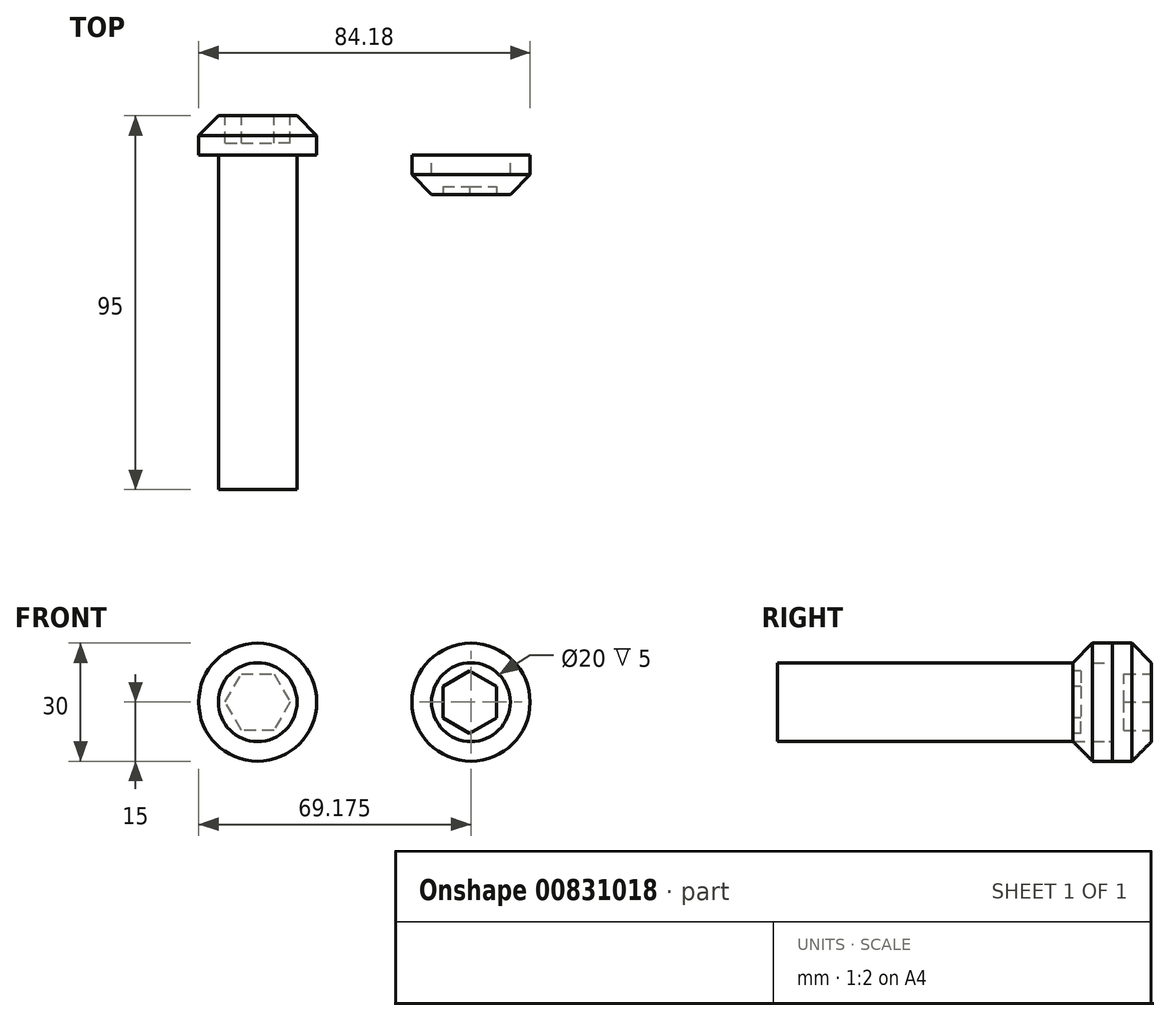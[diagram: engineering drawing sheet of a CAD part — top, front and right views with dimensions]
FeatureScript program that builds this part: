
annotation { "Feature Type Name" : "Feature", "Feature Type Description" : "" }
export const myFeature = defineFeature(function(context is Context, id is Id, definition is map)
    precondition{}
    {
        {
            var Q0;
            Q0=qCreatedBy(makeId("Front.planeOp"),FACE);
            var sketch = newSketch(context, id + "F0", { "sketchPlane" : qUnion([Q0])});
            skCircle(sketch, "E0", {"center": v(0, 0) * mm, "radius": 10 * mm});
            skCircle(sketch, "E1", {"center": v(0, 0) * mm, "radius": 15 * mm});
            skSolve(sketch);
        }
        {
            var Q0;
            Q0=makeQuery(id+"F0.imprint","IMPRINT",FACE,{"disambiguationData":[TD([[makeQuery(id+"F0.imprint","IMPRINT",EDGE,{"derivedFrom":sQuery(id+"F0.wireOp",EDGE,"E0")}),1.0]])]});
            extrude(context, id + "F1", {"entities" : qUnion([Q0]), "depth" : 85 * mm, "offsetDistance" : 25 * mm});
        }
        {
            var Q0;
            Q0 = qSketchRegion(id + "F0", true);
            var Q1;
            Q1=makeQuery(id+"F1.opExtrude","CAP_FACE",FACE,{"disambiguationData":[OSD([sQuery(id+"F0.wireOp",EDGE,"E0")])],"isStart":true});
            extrude(context, id + "F2", {"entities" : qUnion([Q0, Q1]), "operationType" : NewBodyOperationType.ADD, "oppositeDirection" : true, "depth" : 10 * mm, "offsetDistance" : 25 * mm});
        }
        {
            var Q0;
            Q0=qCreatedBy(makeId("Front.planeOp"),FACE);
            var sketch = newSketch(context, id + "F3", { "sketchPlane" : qUnion([Q0])});
            skCircle(sketch, "E2", {"center": v(54.18, 0) * mm, "radius": 10 * mm});
            skCircle(sketch, "E3", {"center": v(54.18, 0) * mm, "radius": 15 * mm});
            skSolve(sketch);
        }
        {
            var Q0;
            Q0=makeQuery(id+"F3.imprint","IMPRINT",FACE,{"disambiguationData":[TD([[makeQuery(id+"F3.imprint","IMPRINT",EDGE,{"derivedFrom":sQuery(id+"F3.wireOp",EDGE,"E2")}),-1.0]])]});
            var Q1;
            Q1=makeQuery(id+"F3.imprint","IMPRINT",FACE,{"disambiguationData":[TD([[makeQuery(id+"F3.imprint","IMPRINT",EDGE,{"derivedFrom":sQuery(id+"F3.wireOp",EDGE,"E2")}),1.0]])]});
            extrude(context, id + "F4", {"entities" : qUnion([Q0, Q1]), "depth" : 10 * mm, "offsetDistance" : 25 * mm});
        }
        {
            var Q0;
            Q0=makeQuery(id+"F3.imprint","IMPRINT",FACE,{"disambiguationData":[TD([[makeQuery(id+"F3.imprint","IMPRINT",EDGE,{"derivedFrom":sQuery(id+"F3.wireOp",EDGE,"E2")}),1.0]])]});
            extrude(context, id + "F5", {"entities" : qUnion([Q0]), "operationType" : NewBodyOperationType.REMOVE, "depth" : 5 * mm, "offsetDistance" : 25 * mm});
        }
        {
            var Q0;
            Q0=makeQuery(id+"F2.opExtrude","CAP_EDGE",EDGE,{"disambiguationData":[OSD([sQuery(id+"F0.wireOp",EDGE,"E1")])],"isStart":false});
            var Q1;
            Q1=makeQuery(id+"F4.opExtrude","CAP_EDGE",EDGE,{"disambiguationData":[OSD([sQuery(id+"F3.wireOp",EDGE,"E3")])],"isStart":false});
            chamfer(context, id + "F6", {"entities" : qUnion([Q0, Q1]), "width" : 5 * mm, "tangentPropagation" : true});
        }
        {
            var Q0;
            Q0=qCreatedBy(makeId("Front.planeOp"),FACE);
            cPlane(context, id + "F7", {"entities" : qUnion([Q0]), "cplaneType" : CPlaneType.OFFSET, "offset" : 10 * mm, "oppositeDirection" : true, "width" : 150 * mm, "height" : 150 * mm});
        }
        {
            var Q0;
            Q0=qCreatedBy(id+"F7.planeOp",FACE);
            var sketch = newSketch(context, id + "F8", { "sketchPlane" : qUnion([Q0])});
            skCircle(sketch, "E4.cCircle", {"center": v(0, 0) * mm, "radius": 7.15 * mm, "construction": true});
            skLineSegment(sketch, "E4.0", {"start": v(-4.13, 7.15) * mm, "end": v(4.13, 7.15) * mm});
            skLineSegment(sketch, "E4.1", {"start": v(4.13, 7.15) * mm, "end": v(8.25, 0) * mm});
            skLineSegment(sketch, "E4.2", {"start": v(8.25, 0) * mm, "end": v(4.13, -7.15) * mm});
            skLineSegment(sketch, "E4.3", {"start": v(4.13, -7.15) * mm, "end": v(-4.13, -7.15) * mm});
            skLineSegment(sketch, "E4.4", {"start": v(-4.13, -7.15) * mm, "end": v(-8.25, 0) * mm});
            skLineSegment(sketch, "E4.5", {"start": v(-8.25, 0) * mm, "end": v(-4.13, 7.15) * mm});
            skPoint(sketch, "E4.0.midPoint", {"position": v(0, 7.15) * mm});
            skSolve(sketch);
        }
        {
            var Q0;
            Q0 = qSketchRegion(id + "F8", true);
            extrude(context, id + "F9", {"entities" : qUnion([Q0]), "operationType" : NewBodyOperationType.REMOVE, "depth" : 7 * mm, "offsetDistance" : 25 * mm});
        }
        {
            var Q0;
            Q0=qCreatedBy(makeId("Front.planeOp"),FACE);
            cPlane(context, id + "F10", {"entities" : qUnion([Q0]), "cplaneType" : CPlaneType.OFFSET, "offset" : 10 * mm, "width" : 150 * mm, "height" : 150 * mm});
        }
        {
            var Q0;
            Q0=qCreatedBy(id+"F10.planeOp",FACE);
            var sketch = newSketch(context, id + "F11", { "sketchPlane" : qUnion([Q0])});
            skCircle(sketch, "E5.cCircle", {"center": v(53.86, 0) * mm, "radius": 6.82 * mm, "construction": true});
            skLineSegment(sketch, "E5.0", {"start": v(60.68, 3.94) * mm, "end": v(60.68, -3.94) * mm});
            skLineSegment(sketch, "E5.1", {"start": v(60.68, -3.94) * mm, "end": v(53.86, -7.88) * mm});
            skLineSegment(sketch, "E5.2", {"start": v(53.86, -7.88) * mm, "end": v(47.03, -3.94) * mm});
            skLineSegment(sketch, "E5.3", {"start": v(47.03, -3.94) * mm, "end": v(47.03, 3.94) * mm});
            skLineSegment(sketch, "E5.4", {"start": v(47.03, 3.94) * mm, "end": v(53.86, 7.88) * mm});
            skLineSegment(sketch, "E5.5", {"start": v(53.86, 7.88) * mm, "end": v(60.68, 3.94) * mm});
            skPoint(sketch, "E5.0.midPoint", {"position": v(60.68, 0) * mm});
            skSolve(sketch);
        }
        {
            var Q0;
            Q0=makeQuery(id+"F11.imprint","IMPRINT",FACE,{"disambiguationData":[TD([[makeQuery(id+"F11.imprint","IMPRINT",EDGE,{"derivedFrom":sQuery(id+"F11.wireOp",EDGE,"E5.0")}),-1.0]])]});
            extrude(context, id + "F12", {"entities" : qUnion([Q0]), "operationType" : NewBodyOperationType.REMOVE, "oppositeDirection" : true, "depth" : 2 * mm, "offsetDistance" : 25 * mm});
        }
    });
